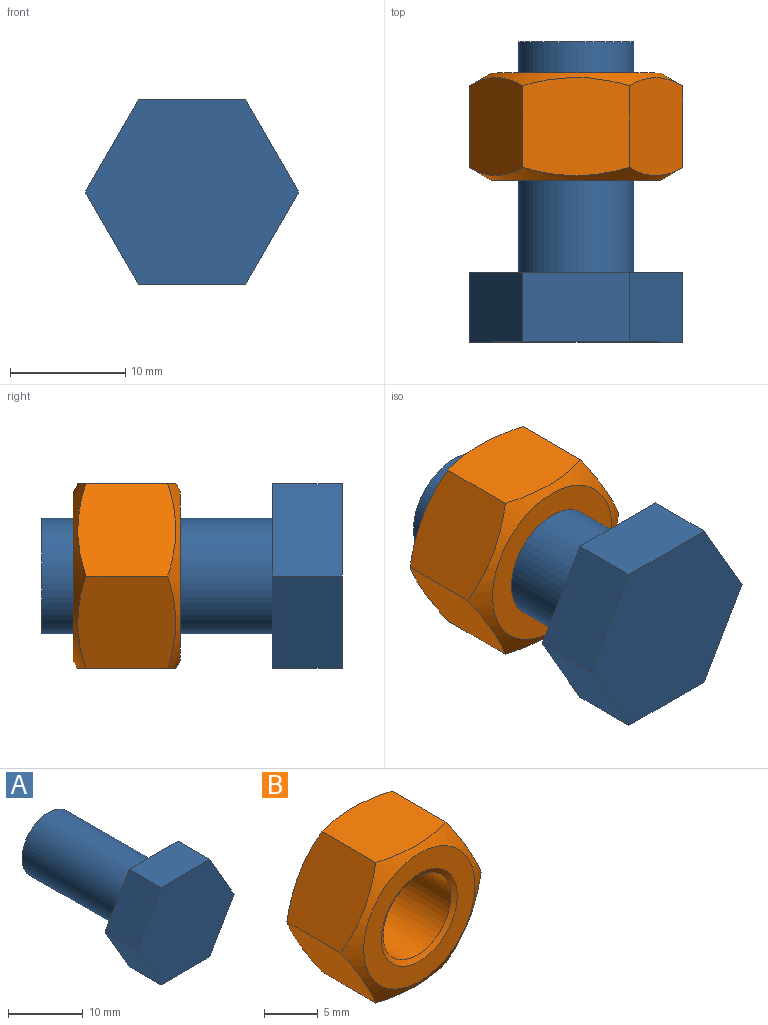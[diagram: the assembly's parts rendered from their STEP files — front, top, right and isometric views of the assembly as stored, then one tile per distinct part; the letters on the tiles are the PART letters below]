
ASSEMBLY  parts=2 mates=1
PART A: 10 faces, bbox 18.5x26x16 mm
  f0: plane 8x6mm, normal (-0.87,0,0.5), area 55.4mm2, adj f1,f5,f6,f7
  f1: plane 8x6mm, normal (-0.87,0,-0.5), area 55.4mm2, adj f0,f2,f6,f7
  f2: plane 9.24x6mm, normal (0,0,-1), area 55.4mm2, adj f1,f3,f6,f7
  f3: plane 8x6mm, normal (0.87,0,-0.5), area 55.4mm2, adj f2,f4,f6,f7
  f4: plane 8x6mm, normal (0.87,0,0.5), area 55.4mm2, adj f3,f5,f6,f7
  f5: plane 9.24x6mm, normal (0,0,1), area 55.4mm2, adj f0,f4,f6,f7
  f6: plane 18.48x16mm, normal (0,-1,0), area 221.7mm2, adj f0,f1,f2,f3,f4,f5
  f7: plane 18.48x16mm, normal (0,1,0), area 143.2mm2, adj f0,f1,f2,f3,f4,f5,f8
  f8: cylinder r=5mm len=20mm, axis (0,-1,0), area 628.3mm2, adj f7,f9
  f9: plane 10x10mm, normal (0,1,0), area 78.5mm2, adj f8
PART B: 13 faces, bbox 19.2x10.1x19.2 mm
  f0: cone r=7.32mm half-angle=60deg, axis (0,-1,0), area 64.2mm2, adj f1,f2,f3,f4,f5,f6,f7
  f1: plane 14.63x14.63mm, normal (0,1,0), area 89.6mm2, adj f0,f10
  f2: plane 8.52x8mm, normal (0.87,0,-0.5), area 74.1mm2, adj f0,f3,f7,f8
  f3: plane 8.52x8mm, normal (0.87,0,0.5), area 74.1mm2, adj f0,f2,f4,f8
  f4: plane 10.01x9.28mm, normal (0,0,1), area 74.1mm2, adj f0,f3,f5,f8
  f5: plane 8.52x8mm, normal (-0.87,0,0.5), area 74.1mm2, adj f0,f4,f6,f8
  f6: plane 8.52x8mm, normal (-0.87,0,-0.5), area 74.1mm2, adj f0,f5,f7,f8
  f7: plane 10.01x9.28mm, normal (0,0,-1), area 74.1mm2, adj f0,f2,f6,f8
  f8: cone r=9.24mm half-angle=60deg, axis (0,1,0), area 64.2mm2, adj f2,f3,f4,f5,f6,f7,f9
  f9: plane 14.63x14.63mm, normal (0,-1,0), area 89.6mm2, adj f8,f12
  f10: cone r=5mm half-angle=60deg, axis (0,1,0), area 18.6mm2, adj f1,f11
  f11: cylinder r=4.46mm len=8.92mm, axis (0,1,0), area 243mm2, adj f10,f12
  f12: cone r=4.46mm half-angle=60deg, axis (0,-1,0), area 18.6mm2, adj f9,f11
PLACE A at identity
PLACE B t=(-57.85,17.3,58.03)mm
MATE fastened B.f8 <-> A.f8  axis (0,-1,0) through (-57.85,8,58.03)mm
